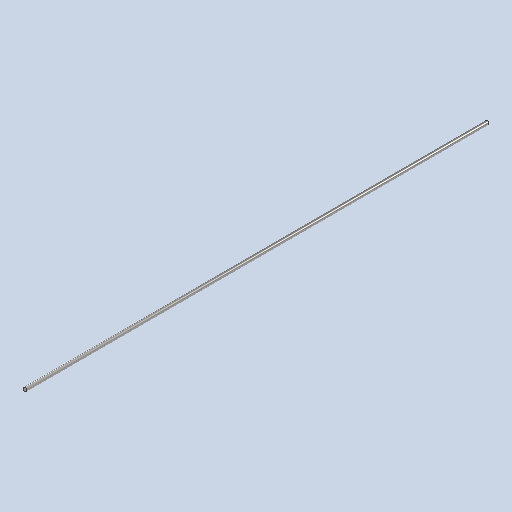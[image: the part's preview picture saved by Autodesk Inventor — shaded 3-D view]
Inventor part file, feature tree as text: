
AUTODESK INVENTOR PART (.ipt)
format: ipt  version: 2025.1 (Build 291241000, 241)  size: 99,328 bytes
history: native  units: mm
features: other x1, extrude x1
ambient origin geometry x8: Origin, YZ Plane, XZ Plane, XY Plane, X Axis, Y Axis, Z Axis, Center Point
bodies: Body1 (feature_tree)
feature tree (2):
  other  "Sólido1"
  extrude  "Extrusão1"  Depth=8.0mm
